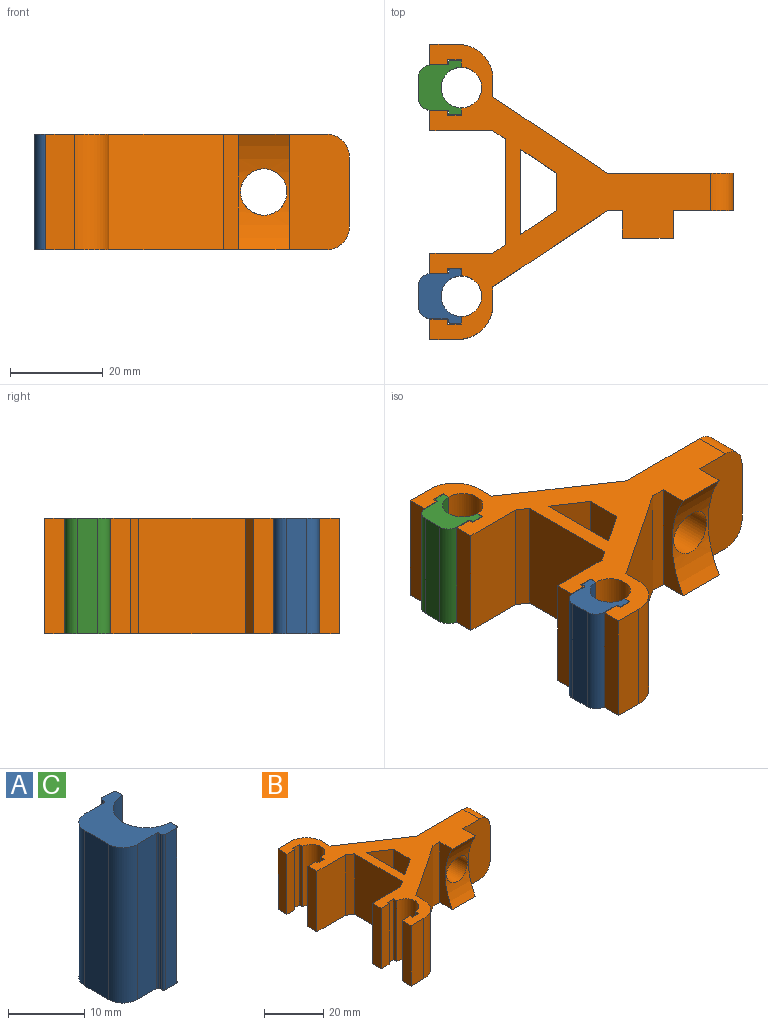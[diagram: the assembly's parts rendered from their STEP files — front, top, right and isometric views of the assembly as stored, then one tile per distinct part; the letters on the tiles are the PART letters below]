
ASSEMBLY  parts=3 mates=2
PART A: 20 faces, bbox 9.3x11.8x25 mm
  f0: plane 25x2.07mm, normal (0,1,0), area 51.9mm2, adj f10,f11,f14,f16
  f1: plane 25x0.32mm, normal (-1,0,0), area 8.1mm2, adj f10,f11,f14,f15
  f2: plane 25x3.51mm, normal (0,1,0), area 87.7mm2, adj f10,f11,f12,f15
  f3: plane 25x4.44mm, normal (-1,0,0), area 111mm2, adj f10,f11,f12,f13
  f4: plane 25x3.51mm, normal (0,-1,0), area 87.7mm2, adj f10,f11,f13,f17
  f5: plane 25x0.32mm, normal (-1,0,0), area 8.1mm2, adj f10,f11,f17,f18
  f6: plane 25x2.07mm, normal (0,-1,0), area 51.9mm2, adj f10,f11,f18,f19
  f7: plane 25x1.16mm, normal (1,0,0), area 29.1mm2, adj f8,f10,f11,f19
  f8: cylinder r=4.38mm len=25mm, axis (0,0,-1), area 343.6mm2, adj f7,f9,f10,f11
  f9: plane 25x1.16mm, normal (1,0,0), area 29.1mm2, adj f8,f10,f11,f16
  f10: plane 11.75x9.25mm, normal (0,0,1), area 62.5mm2, adj f0,f1,f2,f3,f4,f5,f6,f7
  f11: plane 11.75x9.25mm, normal (0,0,-1), area 62.5mm2, adj f0,f1,f2,f3,f4,f5,f6,f7
  f12: cylinder r=2.66mm len=25mm, axis (0,0,-1), area 104.3mm2, adj f2,f3,f10,f11
  f13: cylinder r=2.66mm len=25mm, axis (0,0,1), area 104.3mm2, adj f3,f4,f10,f11
  f14: cylinder r=0.34mm len=25mm, axis (0,0,-1), area 13.3mm2, adj f0,f1,f10,f11
  f15: cylinder r=0.34mm len=25mm, axis (0,0,1), area 13.3mm2, adj f1,f2,f10,f11
  f16: cylinder r=0.34mm len=25mm, axis (0,0,1), area 13.3mm2, adj f0,f9,f10,f11
  f17: cylinder r=0.34mm len=25mm, axis (0,0,1), area 13.3mm2, adj f4,f5,f10,f11
  f18: cylinder r=0.34mm len=25mm, axis (0,0,-1), area 13.3mm2, adj f5,f6,f10,f11
  f19: cylinder r=0.34mm len=25mm, axis (0,0,1), area 13.3mm2, adj f6,f7,f10,f11
PART B: 51 faces, bbox 65.5x63.6x25 mm
  f0: plane 25x2.63mm, normal (-0.56,-0.83,0), area 79mm2, adj f4,f40,f41,f45
  f1: plane 25x2.63mm, normal (-0.56,0.83,0), area 79mm2, adj f8,f40,f41,f45
  f2: plane 25x6mm, normal (1,0,0), area 93mm2, adj f23,f40,f41,f44
  f3: plane 25x3.25mm, normal (0,-1,0), area 81.2mm2, adj f22,f40,f41,f43
  f4: plane 25x13.59mm, normal (0,-1,0), area 339.7mm2, adj f0,f39,f40,f41
  f5: plane 25x7.73mm, normal (-0.56,-0.83,0), area 232.6mm2, adj f6,f40,f41,f46
  f6: plane 25x8mm, normal (-1,0,0), area 200mm2, adj f5,f7,f40,f41
  f7: plane 25x7.73mm, normal (-0.56,0.83,0), area 232.6mm2, adj f6,f40,f41,f46
  f8: plane 25x13.59mm, normal (0,1,0), area 339.7mm2, adj f1,f9,f40,f41
  f9: plane 25x4.3mm, normal (-1,0,0), area 107.4mm2, adj f8,f10,f40,f41
  f10: plane 25x3.79mm, normal (0,-1,0), area 94.9mm2, adj f9,f11,f40,f41
  f11: plane 25x1mm, normal (1,0,0), area 25mm2, adj f10,f12,f40,f41
  f12: plane 25x3mm, normal (0,-1,0), area 75mm2, adj f11,f13,f40,f41
  f13: plane 25x1.63mm, normal (-1,0,0), area 40.6mm2, adj f12,f14,f40,f41
  f14: cylinder r=4.38mm len=25mm, axis (0,0,-1), area 343.6mm2, adj f13,f15,f40,f41
  f15: plane 25x1.63mm, normal (-1,0,0), area 40.6mm2, adj f14,f16,f40,f41
  f16: plane 25x3mm, normal (0,1,0), area 75mm2, adj f15,f17,f40,f41
  f17: plane 25x1mm, normal (1,0,0), area 25mm2, adj f16,f18,f40,f41
  f18: plane 25x3.79mm, normal (0,1,0), area 94.9mm2, adj f17,f19,f40,f41
  f19: plane 25x4.3mm, normal (-1,0,0), area 107.4mm2, adj f18,f20,f40,f41
  f20: plane 25x6.11mm, normal (0,-1,0), area 152.6mm2, adj f19,f40,f41,f48
  f21: plane 25x3.82mm, normal (1,0,0), area 95.4mm2, adj f22,f40,f41,f48
  f22: plane 25x24.66mm, normal (0.56,-0.83,0), area 741.8mm2, adj f3,f21,f40,f41
  f23: plane 25x12.99mm, normal (0,-1,0), area 313.9mm2, adj f2,f24,f40,f41,f49,f50
  f24: plane 15x8mm, normal (1,0,0), area 120mm2, adj f23,f25,f49,f50
  f25: plane 27.23x25mm, normal (0,1,0), area 591.6mm2, adj f24,f26,f40,f41,f42,f49,f50
  f26: plane 25x24.66mm, normal (0.56,0.83,0), area 741.8mm2, adj f25,f27,f40,f41
  f27: plane 25x3.82mm, normal (1,0,0), area 95.4mm2, adj f26,f40,f41,f47
  f28: plane 25x6.11mm, normal (0,1,0), area 152.6mm2, adj f29,f40,f41,f47
  f29: plane 25x4.3mm, normal (-1,0,0), area 107.4mm2, adj f28,f30,f40,f41
  f30: plane 25x3.79mm, normal (0,-1,0), area 94.9mm2, adj f29,f31,f40,f41
  f31: plane 25x1mm, normal (1,0,0), area 25mm2, adj f30,f32,f40,f41
  f32: plane 25x3mm, normal (0,-1,0), area 75mm2, adj f31,f33,f40,f41
  f33: plane 25x1.63mm, normal (-1,0,0), area 40.6mm2, adj f32,f34,f40,f41
  f34: cylinder r=4.38mm len=25mm, axis (0,0,-1), area 343.6mm2, adj f33,f35,f40,f41
  f35: plane 25x1.63mm, normal (-1,0,0), area 40.6mm2, adj f34,f36,f40,f41
  f36: plane 25x3mm, normal (0,1,0), area 75mm2, adj f35,f37,f40,f41
  f37: plane 25x1mm, normal (1,0,0), area 25mm2, adj f36,f38,f40,f41
  f38: plane 25x3.79mm, normal (0,1,0), area 94.9mm2, adj f37,f39,f40,f41
  f39: plane 25x4.3mm, normal (-1,0,0), area 107.4mm2, adj f4,f38,f40,f41
  f40: plane 63.6x60.49mm, normal (0,0,1), area 954.7mm2, adj f0,f1,f2,f3,f4,f5,f6,f7
  f41: plane 63.6x60.49mm, normal (0,0,-1), area 954.7mm2, adj f0,f1,f2,f3,f4,f5,f6,f7
  f42: cylinder r=5mm len=11.14mm, axis (0,-1,0), area 341.8mm2, adj f25,f44
  f43: plane 25x6mm, normal (-1,0,0), area 93mm2, adj f3,f40,f41,f44
  f44: cylinder r=24.85mm len=25mm, axis (1,0,0), area 209.2mm2, adj f2,f40,f41,f42,f43
  f45: plane 25x22.89mm, normal (-1,0,0), area 572.3mm2, adj f0,f1,f40,f41
  f46: plane 25x18.35mm, normal (1,0,0), area 458.6mm2, adj f5,f7,f40,f41
  f47: cylinder r=7.48mm len=25mm, axis (0,0,1), area 293.9mm2, adj f27,f28,f40,f41
  f48: cylinder r=7.48mm len=25mm, axis (0,0,1), area 293.9mm2, adj f20,f21,f40,f41
  f49: cylinder r=5mm len=8mm, axis (0,1,0), area 62.8mm2, adj f23,f24,f25,f41
  f50: cylinder r=5mm len=8mm, axis (0,-1,0), area 62.8mm2, adj f23,f24,f25,f40
PART C: same geometry as A
PLACE A t=(-5.11,-23.03,0)mm
PLACE B at identity fixed
PLACE C t=(-5.11,21.97,0)mm
MATE slider A.f8 <-> B.f14  axis (0,0,1) through (-2.99,-22.5,25)mm
MATE slider C.f8 <-> B.f34  axis (0,0,1) through (-2.99,22.5,25)mm
